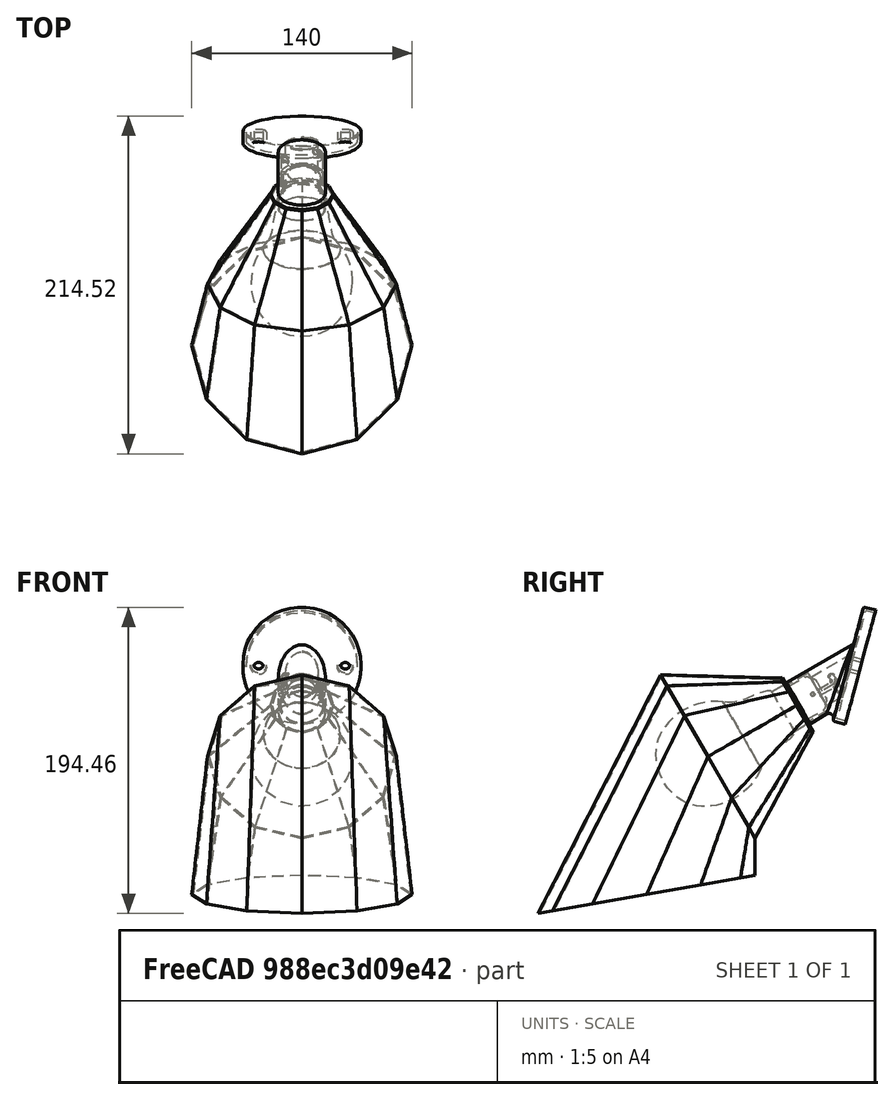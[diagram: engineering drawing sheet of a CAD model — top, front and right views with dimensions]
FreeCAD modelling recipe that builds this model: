
FCSTD DOCUMENT  (FreeCAD 1.0R39285 (Git))
Label: MA_lampshade
License: CERN Open Hardware Licence permissive
LicenseURL: https://cern-ohl.web.cern.ch/
objects: Sketcher::SketchObject×4, PartDesign::Plane×3, Part::Feature×2, Mesh::Feature×2, PartDesign::AdditiveLoft×1, PartDesign::Pad×1, PartDesign::Body×1
note: 20 computed .brp shape members not serialized (recipe doc carries the construction recipe); baked Part::Feature solids carry a one-line shape summary decoded from their .brp

FEATURE [Part::Feature] Part__Feature  label="lamp holder"
  Placement = pos=(0,15.8828,-13.486) rot=(-1,0,0;4.97419rad)
  shape: bbox 81.18 x 57.54 x 78.66 mm, 129 faces (baked)
FEATURE [Mesh::Feature] LampShade_Sails
  Placement = pos=(-126,67.8356,-123.391) rot=(1,0,0;2.35619rad)
FEATURE [Mesh::Feature] LampShade_Crystals
FEATURE [Part::Feature] Part__Feature001  label="Led bulb"
  Placement = pos=(0,0.3575,-28.6681) rot=(-1,0,0;2.61799rad)
  shape: bbox 64.6 x 109.1 x 83.18 mm, 18 faces (baked)
FEATURE [PartDesign::Plane] DatumPlane
  AttachmentOffset = pos=(0,0,40) rot=(1,0,0;0.523599rad)
  AttachmentSupport = -> [XZ_Plane]
  Length = 183.161
  MapMode = 5
  Placement = pos=(0,-40,8.9e-15) rot=(1,0,0;2.0944rad)
  ResizeMode = 0
  Width = 375.818
FEATURE [PartDesign::Plane] DatumPlane001
  AttachmentOffset = pos=(0,0,65) rot=(0,0,1;0rad)
  AttachmentSupport = -> [DatumPlane]
  Length = 183.161
  MapMode = 5
  Placement = pos=(0,-96.2917,-32.5) rot=(1,0,0;2.0944rad)
  ResizeMode = 0
  Width = 375.818
FEATURE [PartDesign::Plane] DatumPlane002
  AttachmentOffset = pos=(0,0,-140) rot=(1,0,0;0.174533rad)
  AttachmentSupport = -> [XY_Plane]
  Length = 180.294
  MapMode = 5
  Placement = pos=(0,0,-140) rot=(1,0,0;0.174533rad)
  ResizeMode = 0
  Width = 330.222
FEATURE [Sketcher::SketchObject] Sketch
  ArcFitTolerance = 1e-06
  AttachmentSupport = -> [DatumPlane]
  FullyConstrained = true
  MakeInternals = false
  MapMode = 5
  Placement = pos=(0,-40,1.07e-14) rot=(1,0,0;2.0944rad)
  sketch-geometry (27):
    g0: Circle [constr] CenterX=0 CenterY=-46 CenterZ=0 NormalX=0 NormalY=0 NormalZ=1 AngleXU=0 Radius=11
    g1: LineSegment StartX=-17.3205 StartY=-36 StartZ=0 EndX=-20 EndY=-46 EndZ=0
    g2: LineSegment StartX=-20 StartY=-46 StartZ=0 EndX=-17.3205 EndY=-56 EndZ=0
    g3: LineSegment StartX=-17.3205 StartY=-56 StartZ=0 EndX=-10 EndY=-63.3205 EndZ=0
    g4: LineSegment StartX=-10 StartY=-63.3205 StartZ=0 EndX=0 EndY=-66 EndZ=0
    g5: LineSegment StartX=0 StartY=-66 StartZ=0 EndX=10 EndY=-63.3205 EndZ=0
    g6: LineSegment StartX=10 StartY=-63.3205 StartZ=0 EndX=17.3205 EndY=-56 EndZ=0
    g7: LineSegment StartX=17.3205 StartY=-56 StartZ=0 EndX=20 EndY=-46 EndZ=0
    g8: LineSegment StartX=20 StartY=-46 StartZ=0 EndX=17.3205 EndY=-36 EndZ=0
    g9: LineSegment StartX=17.3205 StartY=-36 StartZ=0 EndX=10 EndY=-28.6795 EndZ=0
    g10: LineSegment StartX=10 StartY=-28.6795 StartZ=0 EndX=0 EndY=-26 EndZ=0
    g11: LineSegment StartX=0 StartY=-26 StartZ=0 EndX=-10 EndY=-28.6795 EndZ=0
    g12: LineSegment StartX=-10 StartY=-28.6795 StartZ=0 EndX=-17.3205 EndY=-36 EndZ=0
    g13: Circle [constr] CenterX=0 CenterY=-46 CenterZ=0 NormalX=0 NormalY=0 NormalZ=1 AngleXU=0 Radius=20
    g14: LineSegment StartX=-16.4545 StartY=-36.5 StartZ=0 EndX=-19 EndY=-46 EndZ=0
    g15: LineSegment StartX=-19 StartY=-46 StartZ=0 EndX=-16.4545 EndY=-55.5 EndZ=0
    g16: LineSegment StartX=-16.4545 StartY=-55.5 StartZ=0 EndX=-9.5 EndY=-62.4545 EndZ=0
    g17: LineSegment StartX=-9.5 StartY=-62.4545 StartZ=0 EndX=-2.52136e-11 EndY=-65 EndZ=0
    g18: LineSegment StartX=-2.52136e-11 StartY=-65 StartZ=0 EndX=9.5 EndY=-62.4545 EndZ=0
    g19: LineSegment StartX=9.5 StartY=-62.4545 StartZ=0 EndX=16.4545 EndY=-55.5 EndZ=0
    g20: LineSegment StartX=16.4545 StartY=-55.5 StartZ=0 EndX=19 EndY=-46 EndZ=0
    g21: LineSegment StartX=19 StartY=-46 StartZ=0 EndX=16.4545 EndY=-36.5 EndZ=0
    g22: LineSegment StartX=16.4545 StartY=-36.5 StartZ=0 EndX=9.5 EndY=-29.5455 EndZ=0
    g23: LineSegment StartX=9.5 StartY=-29.5455 StartZ=0 EndX=0 EndY=-27 EndZ=0
    g24: LineSegment StartX=0 StartY=-27 StartZ=0 EndX=-9.5 EndY=-29.5455 EndZ=0
    g25: LineSegment StartX=-9.5 StartY=-29.5455 StartZ=0 EndX=-16.4545 EndY=-36.5 EndZ=0
    g26: Circle [constr] CenterX=0 CenterY=-46 CenterZ=0 NormalX=0 NormalY=0 NormalZ=1 AngleXU=0 Radius=19
  constraints (59):
    c: Diameter(g0) = 22
    c: PointOnObject(g0,g-2)
    c: Distance(g0,g-1) = 46
    c: Coincident(g1,g2)
    c: Coincident(g2,g3)
    c: Coincident(g3,g4)
    c: Coincident(g4,g5)
    c: Coincident(g5,g6)
    c: Coincident(g6,g7)
    c: Coincident(g7,g8)
    c: Coincident(g8,g9)
    c: Coincident(g9,g10)
    c: Coincident(g10,g11)
    c: Coincident(g11,g12)
    c: Coincident(g12,g1)
    c: Equal(g1, g2-g12) x11
    c: PointOnObject(g1,g13)
    c: PointOnObject(g2,g13)
    c: PointOnObject(g3,g13)
    c: PointOnObject(g4,g13)
    c: PointOnObject(g5,g13)
    c: PointOnObject(g6,g13)
    c: PointOnObject(g7,g13)
    c: PointOnObject(g8,g13)
    c: PointOnObject(g9,g13)
    c: PointOnObject(g10,g13)
    c: PointOnObject(g11,g13)
    c: PointOnObject(g12,g13)
    c: Coincident(g13,g0)
    c: Diameter(g13) = 40
    c: PointOnObject(g10,g-2)
    c: Coincident(g14,g15)
    c: Coincident(g15,g16)
    c: Coincident(g16,g17)
    c: Coincident(g17,g18)
    c: Coincident(g18,g19)
    c: Coincident(g19,g20)
    c: Coincident(g20,g21)
    c: Coincident(g21,g22)
    c: Coincident(g22,g23)
    c: Coincident(g23,g24)
    c: Coincident(g24,g25)
    c: Coincident(g25,g14)
    c: Equal(g14, g15-g25) x11
    c: PointOnObject(g14,g26)
    c: PointOnObject(g15,g26)
    c: PointOnObject(g16,g26)
    c: PointOnObject(g17,g26)
    c: PointOnObject(g18,g26)
    c: PointOnObject(g19,g26)
    c: PointOnObject(g20,g26)
    c: PointOnObject(g21,g26)
    c: PointOnObject(g22,g26)
    c: PointOnObject(g23,g26)
    c: PointOnObject(g24,g26)
    c: PointOnObject(g25,g26)
    c: Coincident(g26,g0)
    c: PointOnObject(g23,g-2)
    c: Diameter(g26) = 38
FEATURE [Sketcher::SketchObject] Sketch001
  ArcFitTolerance = 1e-06
  AttachmentSupport = -> [DatumPlane001]
  ExternalGeometry = -> [Sketch]
  FullyConstrained = true
  MakeInternals = false
  MapMode = 5
  Placement = pos=(0,-96.2917,-32.5) rot=(1,0,0;2.0944rad)
  sketch-geometry (27):
    g0: LineSegment [constr] StartX=0 StartY=-26 StartZ=0 EndX=0 EndY=-66 EndZ=0
    g1: LineSegment StartX=-60 StartY=-46 StartZ=0 EndX=-51.9615 EndY=-76 EndZ=0
    g2: LineSegment StartX=-51.9615 StartY=-76 StartZ=0 EndX=-30 EndY=-97.9615 EndZ=0
    g3: LineSegment StartX=-30 StartY=-97.9615 StartZ=0 EndX=0 EndY=-106 EndZ=0
    g4: LineSegment StartX=0 StartY=-106 StartZ=0 EndX=30 EndY=-97.9615 EndZ=0
    g5: LineSegment StartX=30 StartY=-97.9615 StartZ=0 EndX=51.9615 EndY=-76 EndZ=0
    g6: LineSegment StartX=51.9615 StartY=-76 StartZ=0 EndX=60 EndY=-46 EndZ=0
    g7: LineSegment StartX=60 StartY=-46 StartZ=0 EndX=51.9615 EndY=-16 EndZ=0
    g8: LineSegment StartX=51.9615 StartY=-16 StartZ=0 EndX=30 EndY=5.96152 EndZ=0
    g9: LineSegment StartX=30 StartY=5.96152 StartZ=0 EndX=0 EndY=14 EndZ=0
    g10: LineSegment StartX=0 StartY=14 StartZ=0 EndX=-30 EndY=5.96152 EndZ=0
    g11: LineSegment StartX=-30 StartY=5.96152 StartZ=0 EndX=-51.9615 EndY=-16 EndZ=0
    g12: LineSegment StartX=-51.9615 StartY=-16 StartZ=0 EndX=-60 EndY=-46 EndZ=0
    g13: Circle [constr] CenterX=0 CenterY=-46 CenterZ=0 NormalX=0 NormalY=0 NormalZ=1 AngleXU=0 Radius=60
    g14: LineSegment StartX=-51.0955 StartY=-16.5 StartZ=0 EndX=-59 EndY=-46 EndZ=0
    g15: LineSegment StartX=-59 StartY=-46 StartZ=0 EndX=-51.0955 EndY=-75.5 EndZ=0
    g16: LineSegment StartX=-51.0955 StartY=-75.5 StartZ=0 EndX=-29.5 EndY=-97.0955 EndZ=0
    g17: LineSegment StartX=-29.5 StartY=-97.0955 StartZ=0 EndX=-3.6e-15 EndY=-105 EndZ=0
    g18: LineSegment StartX=-3.6e-15 StartY=-105 StartZ=0 EndX=29.5 EndY=-97.0955 EndZ=0
    g19: LineSegment StartX=29.5 StartY=-97.0955 StartZ=0 EndX=51.0955 EndY=-75.5 EndZ=0
    g20: LineSegment StartX=51.0955 StartY=-75.5 StartZ=0 EndX=59 EndY=-46 EndZ=0
    g21: LineSegment StartX=59 StartY=-46 StartZ=0 EndX=51.0955 EndY=-16.5 EndZ=0
    g22: LineSegment StartX=51.0955 StartY=-16.5 StartZ=0 EndX=29.5 EndY=5.0955 EndZ=0
    g23: LineSegment StartX=29.5 StartY=5.0955 StartZ=0 EndX=0 EndY=13 EndZ=0
    g24: LineSegment StartX=0 StartY=13 StartZ=0 EndX=-29.5 EndY=5.0955 EndZ=0
    g25: LineSegment StartX=-29.5 StartY=5.0955 StartZ=0 EndX=-51.0955 EndY=-16.5 EndZ=0
    g26: Circle [constr] CenterX=0 CenterY=-46 CenterZ=0 NormalX=0 NormalY=0 NormalZ=1 AngleXU=0 Radius=59
  constraints (58):
    c: Coincident(g0,g-3)
    c: Coincident(g0,g-4)
    c: Coincident(g1,g2)
    c: Coincident(g2,g3)
    c: Coincident(g3,g4)
    c: Coincident(g4,g5)
    c: Coincident(g5,g6)
    c: Coincident(g6,g7)
    c: Coincident(g7,g8)
    c: Coincident(g8,g9)
    c: Coincident(g9,g10)
    c: Coincident(g10,g11)
    c: Coincident(g11,g12)
    c: Coincident(g12,g1)
    c: Equal(g1, g2-g12) x11
    c: PointOnObject(g1,g13)
    c: PointOnObject(g2,g13)
    c: PointOnObject(g3,g13)
    c: PointOnObject(g4,g13)
    c: PointOnObject(g5,g13)
    c: PointOnObject(g6,g13)
    c: PointOnObject(g7,g13)
    c: PointOnObject(g8,g13)
    c: PointOnObject(g9,g13)
    c: PointOnObject(g10,g13)
    c: PointOnObject(g11,g13)
    c: PointOnObject(g12,g13)
    c: Symmetric(g0,g0,g13)
    c: Diameter(g13) = 120
    c: PointOnObject(g9,g-2)
    c: Coincident(g14,g15)
    c: Coincident(g15,g16)
    c: Coincident(g16,g17)
    c: Coincident(g17,g18)
    c: Coincident(g18,g19)
    c: Coincident(g19,g20)
    c: Coincident(g20,g21)
    c: Coincident(g21,g22)
    c: Coincident(g22,g23)
    c: Coincident(g23,g24)
    c: Coincident(g24,g25)
    c: Coincident(g25,g14)
    c: Equal(g14, g15-g25) x11
    c: PointOnObject(g14,g26)
    c: PointOnObject(g15,g26)
    c: PointOnObject(g16,g26)
    c: PointOnObject(g17,g26)
    c: PointOnObject(g18,g26)
    c: PointOnObject(g19,g26)
    c: PointOnObject(g20,g26)
    c: PointOnObject(g21,g26)
    c: PointOnObject(g22,g26)
    c: PointOnObject(g23,g26)
    c: PointOnObject(g24,g26)
    c: PointOnObject(g25,g26)
    c: Coincident(g26,g13)
    c: PointOnObject(g23,g-2)
    c: Diameter(g26) = 118
FEATURE [Sketcher::SketchObject] Sketch002
  ArcFitTolerance = 1e-06
  AttachmentSupport = -> [DatumPlane002]
  FullyConstrained = true
  MakeInternals = false
  MapMode = 5
  Placement = pos=(0,0,-140) rot=(1,0,0;0.174533rad)
  sketch-geometry (26):
    g0: LineSegment StartX=-70 StartY=-114 StartZ=0 EndX=-60.6218 EndY=-149 EndZ=0
    g1: LineSegment StartX=-60.6218 StartY=-149 StartZ=0 EndX=-35 EndY=-174.622 EndZ=0
    g2: LineSegment StartX=-35 StartY=-174.622 StartZ=0 EndX=3.55e-14 EndY=-184 EndZ=0
    g3: LineSegment StartX=3.55e-14 StartY=-184 StartZ=0 EndX=35 EndY=-174.622 EndZ=0
    g4: LineSegment StartX=35 StartY=-174.622 StartZ=0 EndX=60.6218 EndY=-149 EndZ=0
    g5: LineSegment StartX=60.6218 StartY=-149 StartZ=0 EndX=70 EndY=-114 EndZ=0
    g6: LineSegment StartX=70 StartY=-114 StartZ=0 EndX=60.6218 EndY=-79 EndZ=0
    g7: LineSegment StartX=60.6218 StartY=-79 StartZ=0 EndX=35 EndY=-53.3782 EndZ=0
    g8: LineSegment StartX=35 StartY=-53.3782 StartZ=0 EndX=0 EndY=-44 EndZ=0
    g9: LineSegment StartX=0 StartY=-44 StartZ=0 EndX=-35 EndY=-53.3782 EndZ=0
    g10: LineSegment StartX=-35 StartY=-53.3782 StartZ=0 EndX=-60.6218 EndY=-79 EndZ=0
    g11: LineSegment StartX=-60.6218 StartY=-79 StartZ=0 EndX=-70 EndY=-114 EndZ=0
    g12: Circle [constr] CenterX=0 CenterY=-114 CenterZ=0 NormalX=0 NormalY=0 NormalZ=1 AngleXU=0 Radius=70
    g13: LineSegment StartX=-69 StartY=-114 StartZ=0 EndX=-59.7558 EndY=-148.5 EndZ=0
    g14: LineSegment StartX=-59.7558 StartY=-148.5 StartZ=0 EndX=-34.5 EndY=-173.756 EndZ=0
    g15: LineSegment StartX=-34.5 StartY=-173.756 StartZ=0 EndX=4.97e-14 EndY=-183 EndZ=0
    g16: LineSegment StartX=4.97e-14 StartY=-183 StartZ=0 EndX=34.5 EndY=-173.756 EndZ=0
    g17: LineSegment StartX=34.5 StartY=-173.756 StartZ=0 EndX=59.7558 EndY=-148.5 EndZ=0
    g18: LineSegment StartX=59.7558 StartY=-148.5 StartZ=0 EndX=69 EndY=-114 EndZ=0
    g19: LineSegment StartX=69 StartY=-114 StartZ=0 EndX=59.7558 EndY=-79.5 EndZ=0
    g20: LineSegment StartX=59.7558 StartY=-79.5 StartZ=0 EndX=34.5 EndY=-54.2442 EndZ=0
    g21: LineSegment StartX=34.5 StartY=-54.2442 StartZ=0 EndX=0 EndY=-45 EndZ=0
    g22: LineSegment StartX=0 StartY=-45 StartZ=0 EndX=-34.5 EndY=-54.2442 EndZ=0
    g23: LineSegment StartX=-34.5 StartY=-54.2442 StartZ=0 EndX=-59.7558 EndY=-79.5 EndZ=0
    g24: LineSegment StartX=-59.7558 StartY=-79.5 StartZ=0 EndX=-69 EndY=-114 EndZ=0
    g25: Circle [constr] CenterX=0 CenterY=-114 CenterZ=0 NormalX=0 NormalY=0 NormalZ=1 AngleXU=0 Radius=69
  constraints (57):
    c: Coincident(g0,g1)
    c: Coincident(g1,g2)
    c: Coincident(g2,g3)
    c: Coincident(g3,g4)
    c: Coincident(g4,g5)
    c: Coincident(g5,g6)
    c: Coincident(g6,g7)
    c: Coincident(g7,g8)
    c: Coincident(g8,g9)
    c: Coincident(g9,g10)
    c: Coincident(g10,g11)
    c: Coincident(g11,g0)
    c: Equal(g0, g1-g11) x11
    c: PointOnObject(g0,g12)
    c: PointOnObject(g1,g12)
    c: PointOnObject(g2,g12)
    c: PointOnObject(g3,g12)
    c: PointOnObject(g4,g12)
    c: PointOnObject(g5,g12)
    c: PointOnObject(g6,g12)
    c: PointOnObject(g7,g12)
    c: PointOnObject(g8,g12)
    c: PointOnObject(g9,g12)
    c: PointOnObject(g10,g12)
    c: PointOnObject(g11,g12)
    c: PointOnObject(g12,g-2)
    c: Diameter(g12) = 140
    c: PointOnObject(g8,g-2)
    c: Coincident(g13,g14)
    c: Coincident(g14,g15)
    c: Coincident(g15,g16)
    c: Coincident(g16,g17)
    c: Coincident(g17,g18)
    c: Coincident(g18,g19)
    c: Coincident(g19,g20)
    c: Coincident(g20,g21)
    c: Coincident(g21,g22)
    c: Coincident(g22,g23)
    c: Coincident(g23,g24)
    c: Coincident(g24,g13)
    c: Equal(g13, g14-g24) x11
    c: PointOnObject(g13,g25)
    c: PointOnObject(g14,g25)
    c: PointOnObject(g15,g25)
    c: PointOnObject(g16,g25)
    c: PointOnObject(g17,g25)
    c: PointOnObject(g18,g25)
    c: PointOnObject(g19,g25)
    c: PointOnObject(g20,g25)
    c: PointOnObject(g21,g25)
    c: PointOnObject(g22,g25)
    c: PointOnObject(g23,g25)
    c: PointOnObject(g24,g25)
    c: Coincident(g25,g12)
    c: PointOnObject(g21,g-2)
    c: Diameter(g25) = 138
    c: Distance(g12,g-1) = 114
FEATURE [PartDesign::AdditiveLoft] AdditiveLoft
  Closed = false
  Placement = pos=(0,-40,8.9e-15) rot=(1,0,0;2.0944rad)
  Profile = -> Sketch
  Refine = true
  Ruled = true
  Sections = -> [Sketch001,Sketch002]
  Suppressed = false
FEATURE [Sketcher::SketchObject] Sketch003
  ArcFitTolerance = 1e-06
  AttachmentSupport = -> [AdditiveLoft]
  ExternalGeometry = -> [AdditiveLoft]
  FullyConstrained = true
  MakeInternals = false
  MapMode = 5
  Placement = pos=(0,-40,1.07e-14) rot=(-1,0,0;1.0472rad)
  sketch-geometry (14):
    g0: LineSegment StartX=-10 StartY=63.3205 StartZ=0 EndX=-17.3205 EndY=56 EndZ=0
    g1: LineSegment StartX=-17.3205 StartY=56 StartZ=0 EndX=-20 EndY=46 EndZ=0
    g2: LineSegment StartX=-20 StartY=46 StartZ=0 EndX=-17.3205 EndY=36 EndZ=0
    g3: LineSegment StartX=-17.3205 StartY=36 StartZ=0 EndX=-10 EndY=28.6795 EndZ=0
    g4: LineSegment StartX=-10 StartY=28.6795 StartZ=0 EndX=1.96039e-11 EndY=26 EndZ=0
    g5: LineSegment StartX=1.96039e-11 StartY=26 StartZ=0 EndX=10 EndY=28.6795 EndZ=0
    g6: LineSegment StartX=10 StartY=28.6795 StartZ=0 EndX=17.3205 EndY=36 EndZ=0
    g7: LineSegment StartX=17.3205 StartY=36 StartZ=0 EndX=20 EndY=46 EndZ=0
    g8: LineSegment StartX=20 StartY=46 StartZ=0 EndX=17.3205 EndY=56 EndZ=0
    g9: LineSegment StartX=17.3205 StartY=56 StartZ=0 EndX=10 EndY=63.3205 EndZ=0
    g10: LineSegment StartX=10 StartY=63.3205 StartZ=0 EndX=0 EndY=66 EndZ=0
    g11: LineSegment StartX=0 StartY=66 StartZ=0 EndX=-10 EndY=63.3205 EndZ=0
    g12: Circle [constr] CenterX=0 CenterY=46 CenterZ=0 NormalX=0 NormalY=0 NormalZ=1 AngleXU=0 Radius=20
    g13: Circle CenterX=0 CenterY=46 CenterZ=0 NormalX=0 NormalY=0 NormalZ=1 AngleXU=0 Radius=13.5
  constraints (30):
    c: Coincident(g0,g1)
    c: Coincident(g1,g2)
    c: Coincident(g2,g3)
    c: Coincident(g3,g4)
    c: Coincident(g4,g5)
    c: Coincident(g5,g6)
    c: Coincident(g6,g7)
    c: Coincident(g7,g8)
    c: Coincident(g8,g9)
    c: Coincident(g9,g10)
    c: Coincident(g10,g11)
    c: Coincident(g11,g0)
    c: Equal(g0, g1-g11) x11
    c: PointOnObject(g0,g12)
    c: PointOnObject(g1,g12)
    c: PointOnObject(g2,g12)
    c: PointOnObject(g3,g12)
    c: PointOnObject(g4,g12)
    c: PointOnObject(g5,g12)
    c: PointOnObject(g6,g12)
    c: PointOnObject(g7,g12)
    c: PointOnObject(g8,g12)
    c: PointOnObject(g9,g12)
    c: PointOnObject(g10,g12)
    c: PointOnObject(g11,g12)
    c: PointOnObject(g12,g-2)
    c: PointOnObject(g10,g-2)
    c: Coincident(g0,g-3)
    c: Diameter(g13) = 27
    c: Coincident(g13,g12)
FEATURE [PartDesign::Pad] Pad
  BaseFeature = -> AdditiveLoft
  Direction = (0,0.866025,0.5)
  Length = 1
  Length2 = 10
  Placement = pos=(0,-40,8.9e-15) rot=(1,0,0;2.0944rad)
  Profile = -> Sketch003
  ReferenceAxis = -> Sketch003 [N_Axis]
  Refine = true
  Suppressed = false
  Type = 0
FEATURE [PartDesign::Body] Body  label="shade"
  AllowCompound = false
  Group = -> [DatumPlane,DatumPlane001,DatumPlane002,Sketch,Sketch001,Sketch002,AdditiveLoft,Sketch003,Pad]
  Origin = -> Origin
  Tip = -> Pad
